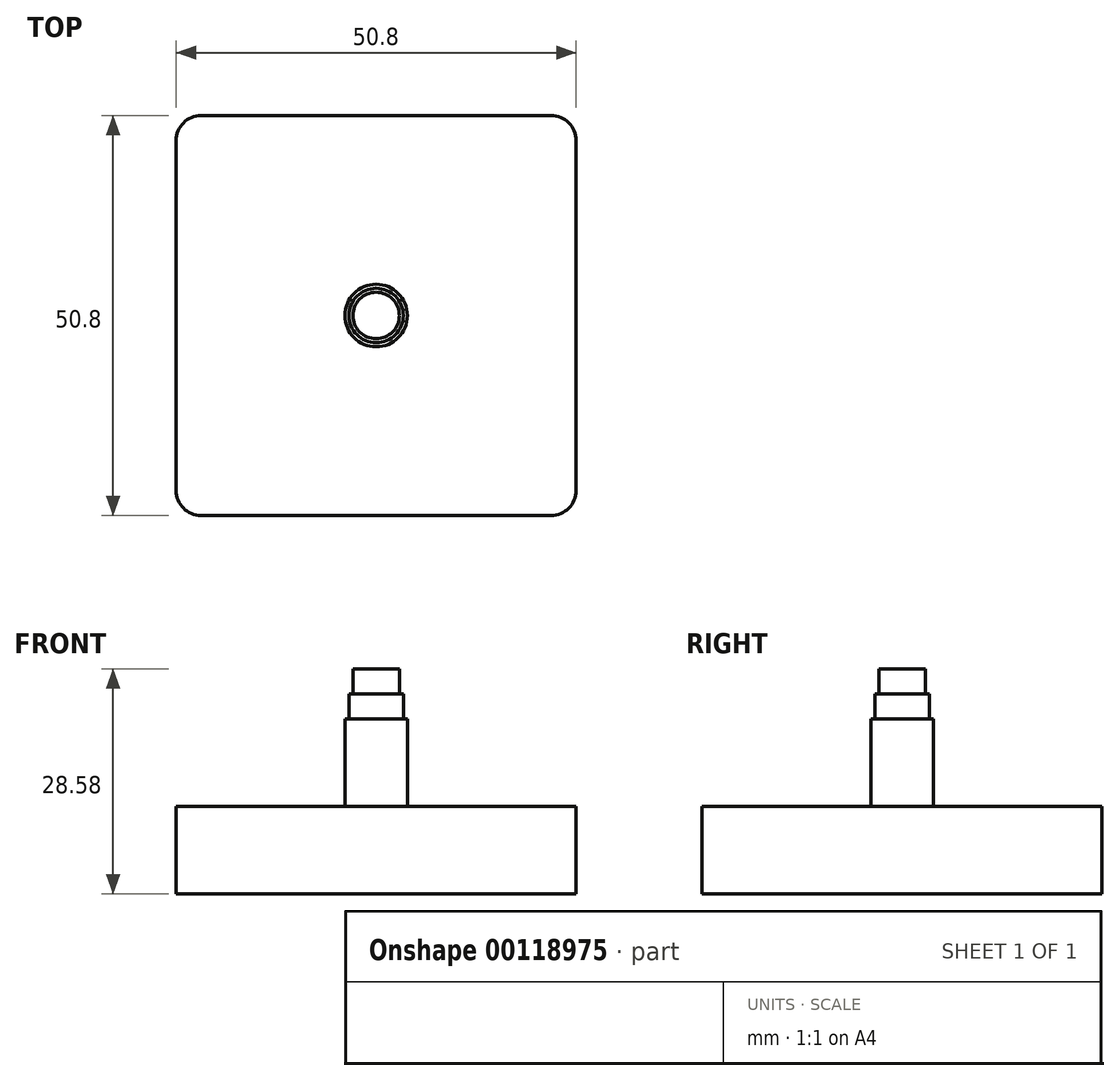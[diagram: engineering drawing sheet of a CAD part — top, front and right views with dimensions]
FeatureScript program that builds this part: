
annotation { "Feature Type Name" : "Feature", "Feature Type Description" : "" }
export const myFeature = defineFeature(function(context is Context, id is Id, definition is map)
    precondition{}
    {
        {
            var Q0;
            Q0=qCreatedBy(makeId("Top.planeOp"),FACE);
            var sketch = newSketch(context, id + "F0", { "sketchPlane" : qUnion([Q0])});
            skLineSegment(sketch, "E0.bottom", {"start": v(-25.4, 25.4) * mm, "end": v(25.4, 25.4) * mm});
            skLineSegment(sketch, "E0.top", {"start": v(-25.4, -25.4) * mm, "end": v(25.4, -25.4) * mm});
            skLineSegment(sketch, "E0.left", {"start": v(-25.4, 25.4) * mm, "end": v(-25.4, -25.4) * mm});
            skLineSegment(sketch, "E0.right", {"start": v(25.4, 25.4) * mm, "end": v(25.4, -25.4) * mm});
            skPoint(sketch, "E0.middle", {"position": v(0, 0) * mm});
            skSolve(sketch);
        }
        {
            var Q0;
            Q0 = qSketchRegion(id + "F0", true);
            extrude(context, id + "F1", {"entities" : qUnion([Q0]), "depth" : 11.1 * mm});
        }
        {
            var Q0;
            Q0=makeQuery(id+"F1.opExtrude","SWEPT_EDGE",EDGE,{"disambiguationData":[OSD([sQuery(id+"F0.wireOp",EDGE,"E0.top"),sQuery(id+"F0.wireOp",EDGE,"E0.right")])]});
            var Q1;
            Q1=makeQuery(id+"F1.opExtrude","SWEPT_EDGE",EDGE,{"disambiguationData":[OSD([sQuery(id+"F0.wireOp",EDGE,"E0.bottom"),sQuery(id+"F0.wireOp",EDGE,"E0.right")])]});
            var Q2;
            Q2=makeQuery(id+"F1.opExtrude","SWEPT_EDGE",EDGE,{"disambiguationData":[OSD([sQuery(id+"F0.wireOp",EDGE,"E0.top"),sQuery(id+"F0.wireOp",EDGE,"E0.left")])]});
            var Q3;
            Q3=makeQuery(id+"F1.opExtrude","SWEPT_EDGE",EDGE,{"disambiguationData":[OSD([sQuery(id+"F0.wireOp",EDGE,"E0.bottom"),sQuery(id+"F0.wireOp",EDGE,"E0.left")])]});
            fillet(context, id + "F2", {"entities" : qUnion([Q0, Q1, Q2, Q3]), "radius" : 3.17 * mm, "tangentPropagation" : true, "allowEdgeOverflow" : false});
        }
        {
            var Q0;
            Q0=makeQuery(id+"F1.opExtrude","CAP_FACE",FACE,{"disambiguationData":[OSD([sQuery(id+"F0.wireOp",EDGE,"E0.bottom"),sQuery(id+"F0.wireOp",EDGE,"E0.top"),sQuery(id+"F0.wireOp",EDGE,"E0.left"),sQuery(id+"F0.wireOp",EDGE,"E0.right")])],"isStart":false});
            var sketch = newSketch(context, id + "F3", { "sketchPlane" : qUnion([Q0])});
            skCircle(sketch, "E1", {"center": v(0, 0) * mm, "radius": 3.97 * mm});
            skSolve(sketch);
        }
        {
            var Q0;
            Q0=makeQuery(id+"F3.imprint","IMPRINT",FACE,{"disambiguationData":[TD([[makeQuery(id+"F3.imprint","IMPRINT",EDGE,{"derivedFrom":sQuery(id+"F3.wireOp",EDGE,"E1")}),1.0]])]});
            var Q1;
            Q1=sQuery(id+"F3.wireOp",EDGE,"E1");
            extrude(context, id + "F4", {"entities" : qUnion([Q0]), "surfaceEntities" : qUnion([Q1]), "depth" : 11.1 * mm});
        }
        {
            var Q0;
            Q0=makeQuery(id+"F4.opExtrude","CAP_FACE",FACE,{"disambiguationData":[OSD([sQuery(id+"F3.wireOp",EDGE,"E1")])],"isStart":false});
            var sketch = newSketch(context, id + "F5", { "sketchPlane" : qUnion([Q0])});
            skCircle(sketch, "E2", {"center": v(0, 0) * mm, "radius": 3.46 * mm});
            skSolve(sketch);
        }
        {
            var Q0;
            Q0 = qSketchRegion(id + "F5", true);
            extrude(context, id + "F6", {"entities" : qUnion([Q0]), "operationType" : NewBodyOperationType.ADD, "depth" : 3.17 * mm});
        }
        {
            var Q0;
            Q0=makeQuery(id+"F6.opExtrude","CAP_FACE",FACE,{"disambiguationData":[OSD([sQuery(id+"F5.wireOp",EDGE,"E2")])],"isStart":false});
            var sketch = newSketch(context, id + "F7", { "sketchPlane" : qUnion([Q0])});
            skCircle(sketch, "E3", {"center": v(0, 0) * mm, "radius": 2.95 * mm});
            skSolve(sketch);
        }
        {
            var Q0;
            Q0 = qSketchRegion(id + "F7", true);
            extrude(context, id + "F8", {"entities" : qUnion([Q0]), "operationType" : NewBodyOperationType.ADD, "depth" : 3.17 * mm});
        }
    });
